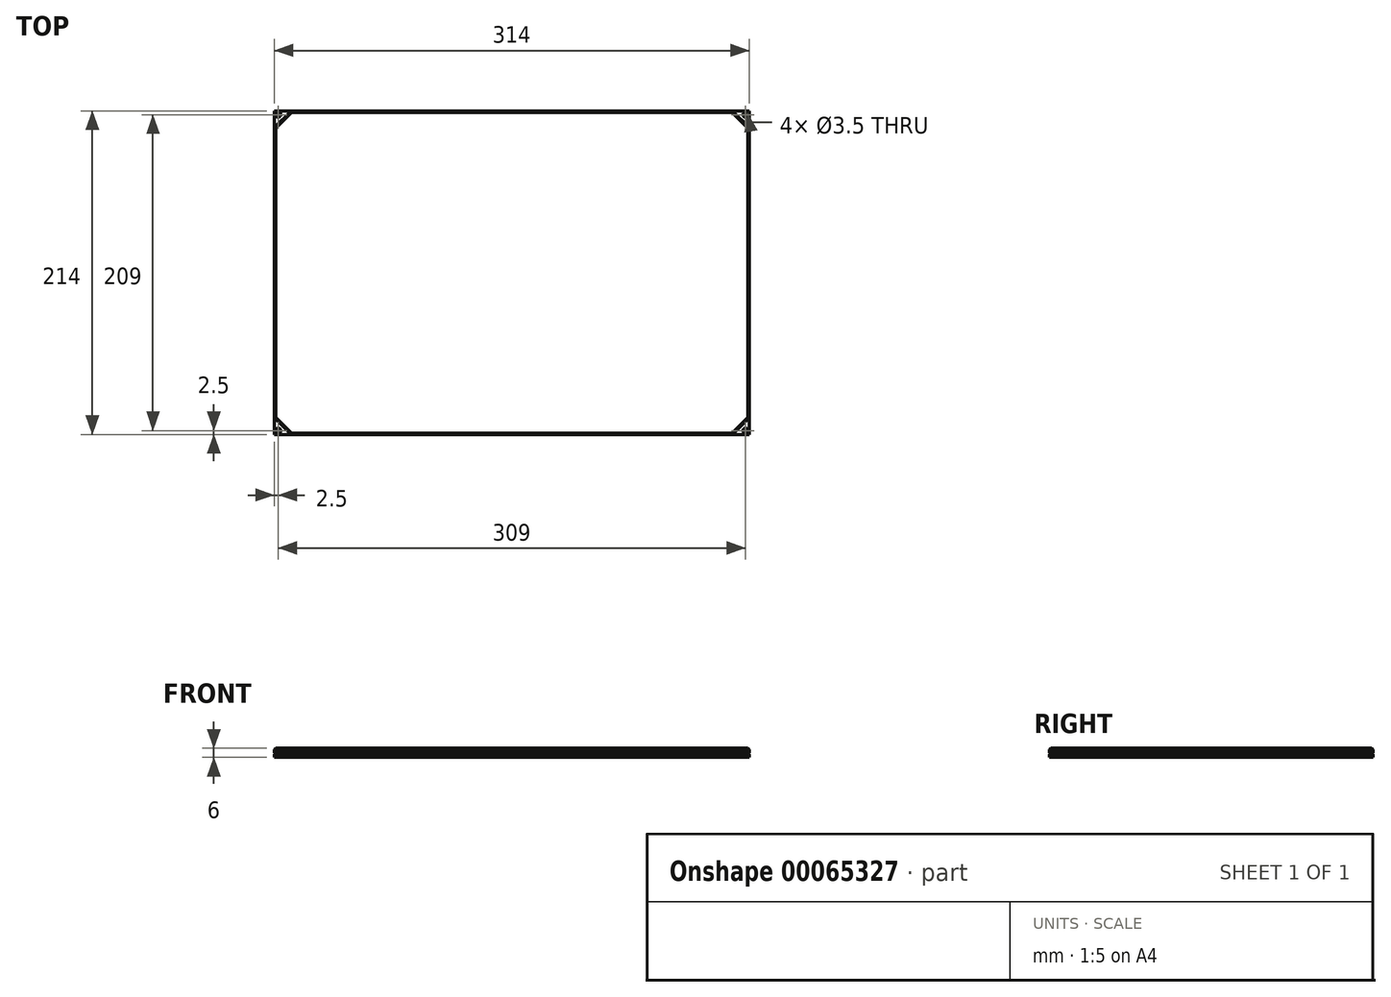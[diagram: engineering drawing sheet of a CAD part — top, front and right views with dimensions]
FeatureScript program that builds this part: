
annotation { "Feature Type Name" : "Feature", "Feature Type Description" : "" }
export const myFeature = defineFeature(function(context is Context, id is Id, definition is map)
    precondition{}
    {
        {
            var Q0;
            Q0=qCreatedBy(makeId("Top.planeOp"),FACE);
            var sketch = newSketch(context, id + "F0", { "sketchPlane" : qUnion([Q0])});
            skLineSegment(sketch, "E0.rect.bottom", {"start": v(157, -107) * mm, "end": v(146, -107) * mm, "construction": true});
            skLineSegment(sketch, "E0.rect.top", {"start": v(157, 107) * mm, "end": v(146, 107) * mm, "construction": true});
            skLineSegment(sketch, "E0.rect.left", {"start": v(157, -107) * mm, "end": v(157, -96) * mm, "construction": true});
            skLineSegment(sketch, "E0.rect.right", {"start": v(-157, -107) * mm, "end": v(-157, -96) * mm, "construction": true});
            skPoint(sketch, "E0.rect.middle", {"position": v(0, 0) * mm});
            skLineSegment(sketch, "E1", {"start": v(-157, 96) * mm, "end": v(-146, 107) * mm});
            skLineSegment(sketch, "E2", {"start": v(-146, 107) * mm, "end": v(146, 107) * mm});
            skLineSegment(sketch, "E3", {"start": v(146, 107) * mm, "end": v(157, 96) * mm});
            skLineSegment(sketch, "E4", {"start": v(157, 96) * mm, "end": v(157, -96) * mm});
            skLineSegment(sketch, "E5", {"start": v(157, -96) * mm, "end": v(146, -107) * mm});
            skLineSegment(sketch, "E6", {"start": v(146, -107) * mm, "end": v(-146, -107) * mm});
            skLineSegment(sketch, "E7", {"start": v(-146, -107) * mm, "end": v(-157, -96) * mm});
            skLineSegment(sketch, "E8", {"start": v(-157, -96) * mm, "end": v(-157, 96) * mm});
            skLineSegment(sketch, "E9", {"start": v(-146, 107) * mm, "end": v(-157, 107) * mm, "construction": true});
            skLineSegment(sketch, "E10", {"start": v(-157, 96) * mm, "end": v(-157, 107) * mm, "construction": true});
            skLineSegment(sketch, "E11", {"start": v(-146, -107) * mm, "end": v(-157, -107) * mm, "construction": true});
            skLineSegment(sketch, "E12", {"start": v(157, -96) * mm, "end": v(157, 96) * mm, "construction": true});
            skLineSegment(sketch, "E13", {"start": v(146, 107) * mm, "end": v(-146, 107) * mm, "construction": true});
            skLineSegment(sketch, "E14", {"start": v(-157, -96) * mm, "end": v(-157, 96) * mm, "construction": true});
            skLineSegment(sketch, "E15", {"start": v(146, -107) * mm, "end": v(-146, -107) * mm, "construction": true});
            skLineSegment(sketch, "E16", {"start": v(157, 96) * mm, "end": v(157, 107) * mm, "construction": true});
            skSolve(sketch);
        }
        {
            var Q0;
            Q0=makeQuery(id+"F0.imprint","IMPRINT",FACE,{"disambiguationData":[TD([[makeQuery(id+"F0.imprint","IMPRINT",EDGE,{"derivedFrom":sQuery(id+"F0.wireOp",EDGE,"E1")}),-1.0]])]});
            extrude(context, id + "F1", {"entities" : qUnion([Q0]), "depth" : 4 * mm});
        }
        {
            var Q0;
            Q0=makeQuery(id+"F1.opExtrude","CAP_FACE",FACE,{"disambiguationData":[OSD([sQuery(id+"F0.wireOp",EDGE,"E1"),sQuery(id+"F0.wireOp",EDGE,"E2"),sQuery(id+"F0.wireOp",EDGE,"E3"),sQuery(id+"F0.wireOp",EDGE,"E4"),sQuery(id+"F0.wireOp",EDGE,"E5"),sQuery(id+"F0.wireOp",EDGE,"E6"),sQuery(id+"F0.wireOp",EDGE,"E7"),sQuery(id+"F0.wireOp",EDGE,"E8")])],"isStart":true});
            var sketch = newSketch(context, id + "F2", { "sketchPlane" : qUnion([Q0])});
            skLineSegment(sketch, "E17.rect.bottom", {"start": v(157, -107) * mm, "end": v(-157, -107) * mm});
            skLineSegment(sketch, "E17.rect.top", {"start": v(157, 107) * mm, "end": v(-157, 107) * mm});
            skLineSegment(sketch, "E17.rect.left", {"start": v(157, -107) * mm, "end": v(157, 107) * mm});
            skLineSegment(sketch, "E17.rect.right", {"start": v(-157, -107) * mm, "end": v(-157, 107) * mm});
            skPoint(sketch, "E17.rect.middle", {"position": v(0, 0) * mm});
            skLineSegment(sketch, "E18.rect.bottom", {"start": v(154.5, -104.5) * mm, "end": v(-154.5, -104.5) * mm, "construction": true});
            skLineSegment(sketch, "E18.rect.top", {"start": v(154.5, 104.5) * mm, "end": v(-154.5, 104.5) * mm, "construction": true});
            skLineSegment(sketch, "E18.rect.left", {"start": v(154.5, -104.5) * mm, "end": v(154.5, 104.5) * mm, "construction": true});
            skLineSegment(sketch, "E18.rect.right", {"start": v(-154.5, -104.5) * mm, "end": v(-154.5, 104.5) * mm, "construction": true});
            skCircle(sketch, "E19", {"center": v(-154.5, 104.5) * mm, "radius": 1.75 * mm});
            skCircle(sketch, "E20", {"center": v(154.5, 104.5) * mm, "radius": 1.75 * mm});
            skCircle(sketch, "E21", {"center": v(154.5, -104.5) * mm, "radius": 1.75 * mm});
            skCircle(sketch, "E22", {"center": v(-154.5, -104.5) * mm, "radius": 1.75 * mm});
            skSolve(sketch);
        }
        {
            var Q0;
            Q0=qSketchRegion(id+"F2",true);
            extrude(context, id + "F3", {"entities" : qUnion([Q0]), "depth" : 2 * mm});
        }
        {
            var Q0;
            Q0=makeQuery(id+"F1.opExtrude","CAP_FACE",FACE,{"disambiguationData":[OSD([sQuery(id+"F0.wireOp",EDGE,"E1"),sQuery(id+"F0.wireOp",EDGE,"E2"),sQuery(id+"F0.wireOp",EDGE,"E3"),sQuery(id+"F0.wireOp",EDGE,"E4"),sQuery(id+"F0.wireOp",EDGE,"E5"),sQuery(id+"F0.wireOp",EDGE,"E6"),sQuery(id+"F0.wireOp",EDGE,"E7"),sQuery(id+"F0.wireOp",EDGE,"E8")])],"isStart":false});
            var Q1;
            Q1=makeQuery(id+"F1.opExtrude","CAP_FACE",FACE,{"disambiguationData":[OSD([sQuery(id+"F0.wireOp",EDGE,"E1"),sQuery(id+"F0.wireOp",EDGE,"E2"),sQuery(id+"F0.wireOp",EDGE,"E3"),sQuery(id+"F0.wireOp",EDGE,"E4"),sQuery(id+"F0.wireOp",EDGE,"E5"),sQuery(id+"F0.wireOp",EDGE,"E6"),sQuery(id+"F0.wireOp",EDGE,"E7"),sQuery(id+"F0.wireOp",EDGE,"E8")])],"isStart":true});
            chamfer(context, id + "F4", {"entities" : qUnion([Q0, Q1]), "width" : 1 * mm, "tangentPropagation" : true});
        }
    });
